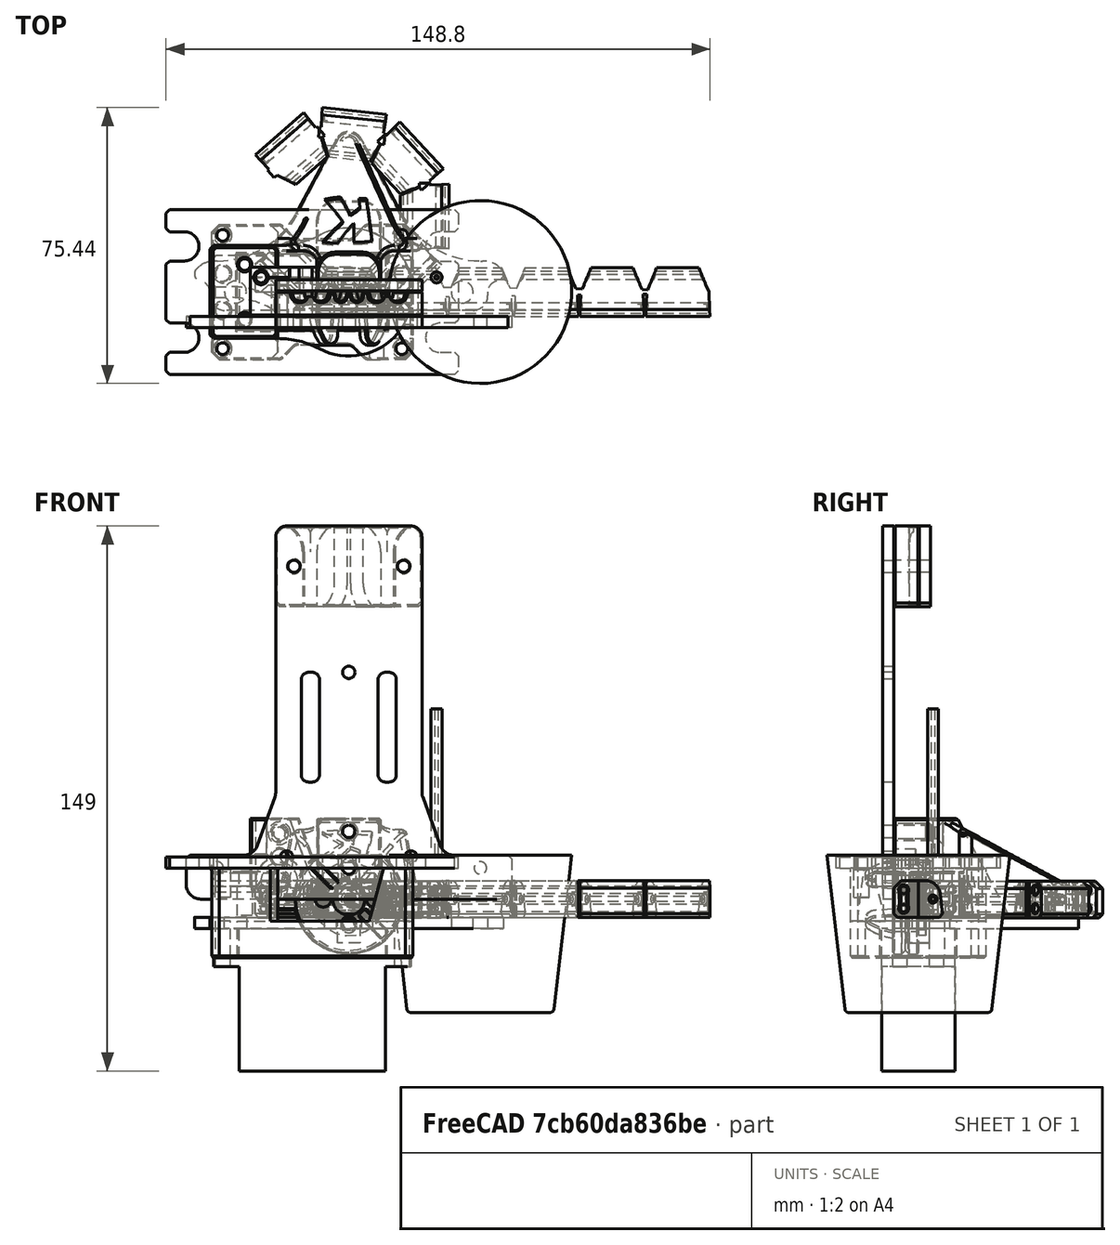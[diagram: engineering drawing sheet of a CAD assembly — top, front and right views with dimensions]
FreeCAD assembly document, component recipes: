
FREECAD ASSEMBLY — COMPONENT RECIPES ("finger-filaflex")

This assembly document has 2 components, labeled P0..P1 below (a component is one placed body or linked part). 1 of them carries a construction recipe — the FreeCAD feature program that regenerates the part from scratch, quoted from this document or its linked companion documents; the rest are supplied as boundary geometry only. No exploded tour is included for this assembly.
COMPONENT P0 — geometry summary ("EnsembleServo"; no construction recipe available for this part):
  bounding box: 80.0 x 61.5 x 45.0 mm
  tessellated surface: 38,648 triangles
  volume: 61605 mm^3 (28% of its bounding box)
COMPONENT P1 — recipe-attached ("finger-actuator", modeled in this document).
Construction recipe (the document's own serialized feature program — sketch geometry with constraints, then the solid features built on it; lengths are millimeters unless a unit is written):

FEATURE [Part::SubShapeBinder] Import004  label="Import004(Chamfer019)"
  BindCopyOnChange = 0
  BindMode = 0
  ClaimChildren = false
  Context = -> <external main-actuator.FCStd>#Part [Part005.Part003.Link008.Body011.Import004.]
  EdgeTolerance = 1e-06
  FillStyle = 0
  FixShape = 1
  Fuse = false
  InvalidShape = false
  MakeFace = false
  MergeEdges = true
  OffsetFill = false
  OffsetIntersection = false
  OffsetJoinType = 0
  OffsetOpenResult = false
  Outline = false
  PartialLoad = false
  Relative = true
  SplitEdges = false
  Support = -> [Part004[Body001.Chamfer019.]]
  TightBound = false
  TreeRank = 344
  ValidateShape = false
  _Version = 8
FEATURE [Sketcher::SketchObject] Sketch037
  ArcFitTolerance = 1e-06
  AttachmentSupport = -> [XZ_Plane016]
  ExternalBSplineMaxDegree = 5
  ExternalBSplineTolerance = 0.0001
  ExternalGeometry = -> [Import004]
  FixShape = 1
  FullyConstrained = true
  InternalTolerance = 1e-06
  InvalidShape = false
  MakeInternals = false
  MapMode = 5
  Placement = pos=(0,0,0) rot=(1,0,0;1.5708rad)
  Support = -> [XZ_Plane016]
  TreeRank = 343
  ValidateShape = false
  sketch-geometry (19):
    g0: LineSegment StartX=-44.5 StartY=0 StartZ=0 EndX=-44.5 EndY=12 EndZ=0
    g1: LineSegment StartX=-44.5 StartY=12 StartZ=0 EndX=-26 EndY=12 EndZ=0
    g2: LineSegment StartX=-26 StartY=12 StartZ=0 EndX=-20 EndY=28.4849 EndZ=0
    g3: LineSegment StartX=-20 StartY=28.4849 StartZ=0 EndX=-20 EndY=102 EndZ=0
    g4: LineSegment StartX=-20 StartY=102 StartZ=0 EndX=20 EndY=102 EndZ=0
    g5: LineSegment StartX=20 StartY=102 StartZ=0 EndX=20 EndY=28.4849 EndZ=0
    g6: LineSegment StartX=20 StartY=28.4849 StartZ=0 EndX=26 EndY=12 EndZ=0
    g7: LineSegment StartX=26 StartY=12 StartZ=0 EndX=44.5 EndY=12 EndZ=0
    g8: LineSegment StartX=44.5 StartY=12 StartZ=0 EndX=44.5 EndY=0 EndZ=0
    g9: LineSegment StartX=44.5 StartY=0 StartZ=0 EndX=-44.5 EndY=0 EndZ=0
    g10: Circle CenterX=0 CenterY=18.5 CenterZ=0 NormalX=0 NormalY=0 NormalZ=1 AngleXU=0 Radius=1.7
    g11: Circle CenterX=0 CenterY=8.5 CenterZ=0 NormalX=0 NormalY=0 NormalZ=1 AngleXU=0 Radius=1.7
    g12: Circle CenterX=17 CenterY=11.5 CenterZ=0 NormalX=0 NormalY=0 NormalZ=1 AngleXU=0 Radius=1.7
    g13: Circle CenterX=-17 CenterY=11.5 CenterZ=0 NormalX=0 NormalY=0 NormalZ=1 AngleXU=0 Radius=1.7
    g14: Circle CenterX=-36 CenterY=8.5 CenterZ=0 NormalX=0 NormalY=0 NormalZ=1 AngleXU=0 Radius=1.7
    g15: Circle CenterX=36 CenterY=8.5 CenterZ=0 NormalX=0 NormalY=0 NormalZ=1 AngleXU=0 Radius=1.7
    g16: Circle CenterX=0 CenterY=62 CenterZ=0 NormalX=0 NormalY=0 NormalZ=1 AngleXU=0 Radius=1.7
    g17: Circle CenterX=-15 CenterY=91 CenterZ=0 NormalX=0 NormalY=0 NormalZ=1 AngleXU=0 Radius=1.7
    g18: Circle CenterX=15 CenterY=91 CenterZ=0 NormalX=0 NormalY=0 NormalZ=1 AngleXU=0 Radius=1.7
  constraints (49):
    c: Vertical(g0)
    c: Coincident(g1,g0)
    c: Horizontal(g1)
    c: Coincident(g1,g2)
    c: Coincident(g2,g3)
    c: Vertical(g3)
    c: Coincident(g3,g4)
    c: Horizontal(g4)
    c: Coincident(g4,g5)
    c: Coincident(g5,g6)
    c: Coincident(g6,g7)
    c: Horizontal(g7)
    c: Coincident(g7,g8)
    c: Vertical(g8)
    c: Coincident(g8,g9)
    c: Coincident(g9,g0)
    c: Horizontal(g9)
    c: Symmetric(g0,g8,g-1)
    c: Symmetric(g1,g6,g-2)
    c: Symmetric(g2,g5,g-2)
    c: Vertical(g5)
    c: DistanceY(g-1,g1) = 12
    c: Angle(g2,g1) = 1.91986
    c: DistanceX(g0,g1) = 18.5
    c: DistanceX(g0,g-1) = 44.5
    c: PointOnObject(g10,g-2)
    c: PointOnObject(g11,g-2)
    c: Equal(g15,g12)
    c: Equal(g15,g10)
    c: Equal(g15,g11)
    c: Equal(g15,g13)
    c: Equal(g15,g14)
    c: Diameter(g15) = 3.4
    c: Symmetric(g13,g12,g-2)
    c: Symmetric(g14,g15,g-2)
    c: DistanceY(g11,g10) = 10
    c: DistanceY(g-1,g11) = 8.5
    c: Coincident(g14,g-3)
    c: Coincident(g13,g-4)
    c: PointOnObject(g16,g-2)
    c: Equal(g18,g17)
    c: Equal(g17,g16)
    c: Equal(g16,g12)
    c: Symmetric(g17,g18,g-2)
    c: DistanceX(g17,g18) = 30
    c: DistanceY(g16,g18) = 29
    c: DistanceY(g18,g4) = 11
    c: DistanceY(g-1,g4) = 102
    c: DistanceX(g4,g4) = 40
FEATURE [PartDesign::Pad] Pad012
  AddSubType = 0
  AlongSketchNormal = false
  AutoTaperInnerAngle = true
  CheckUpToFaceLimits = true
  ClaimChildren = false
  Direction = (0,-1,-2e-16)
  Fit = 0
  FitJoin = 0
  FixShape = 1
  InnerFit = 0
  InnerFitJoin = 0
  InvalidShape = false
  Length = 3
  Length2 = 10
  Linearize = true
  NewSolid = false
  Profile = -> Sketch037
  ReferenceAxis = -> Sketch037 [N_Axis]
  Refine = true
  Suppress = false
  TaperInnerAngle = 0
  TaperInnerAngleRev = 0
  TreeRank = 345
  Type = 0
  ValidateShape = false
  _ProfileBasedVersion = 1
FEATURE [PartDesign::Fillet] Fillet007
  AddSubType = 0
  Base = -> Pad012 [Edge26,Edge1]
  BaseFeature = -> Pad012
  FixShape = 1
  InvalidShape = false
  NewSolid = false
  Radius = 4
  Refine = true
  SupportTransform = false
  Suppress = false
  TreeRank = 346
  UseAllEdges = false
  ValidateShape = false
FEATURE [PartDesign::Fillet] Fillet008
  AddSubType = 0
  Base = -> Fillet007 [Edge54,Edge53,Edge48,Edge27]
  BaseFeature = -> Fillet007
  FixShape = 1
  InvalidShape = false
  NewSolid = false
  Radius = 4
  Refine = true
  SupportTransform = false
  Suppress = false
  TreeRank = 347
  UseAllEdges = false
  ValidateShape = false
FEATURE [PartDesign::Chamfer] Chamfer024
  AddSubType = 0
  Angle = 45
  Base = -> Fillet008 [Edge47,Edge27]
  BaseFeature = -> Fillet008
  ChamferType = 0
  FixShape = 1
  FlipDirection = false
  InvalidShape = false
  NewSolid = false
  Refine = true
  Size = 1
  Size2 = 1
  SupportTransform = false
  Suppress = false
  TreeRank = 348
  UseAllEdges = false
  ValidateShape = false
FEATURE [PartDesign::Fillet] Fillet012
  AddSubType = 0
  Base = -> Chamfer024 [Edge49,Edge45]
  BaseFeature = -> Chamfer024
  FixShape = 1
  InvalidShape = false
  NewSolid = false
  Radius = 3
  Refine = true
  SupportTransform = false
  Suppress = false
  TreeRank = 410
  UseAllEdges = false
  ValidateShape = false
FEATURE [Sketcher::SketchObject] Sketch040
  ArcFitTolerance = 1e-06
  AttachmentSupport = -> [XZ_Plane016]
  ExternalBSplineMaxDegree = 5
  ExternalBSplineTolerance = 0.0001
  ExternalGeometry = -> [Fillet012]
  FixShape = 1
  FullyConstrained = true
  InternalTolerance = 1e-06
  InvalidShape = false
  MakeInternals = false
  MapMode = 5
  Placement = pos=(0,0,0) rot=(1,0,0;1.5708rad)
  Support = -> [XZ_Plane016]
  TreeRank = 411
  ValidateShape = false
  sketch-geometry (10):
    g0: LineSegment StartX=13 StartY=32 StartZ=0 EndX=13 EndY=62 EndZ=0
    g1: LineSegment StartX=13 StartY=62 StartZ=0 EndX=8 EndY=62 EndZ=0
    g2: LineSegment StartX=8 StartY=62 StartZ=0 EndX=8 EndY=32 EndZ=0
    g3: LineSegment StartX=8 StartY=32 StartZ=0 EndX=13 EndY=32 EndZ=0
    g4: GeomPoint [constr] X=10.5 Y=47 Z=0
    g5: LineSegment StartX=-8 StartY=32 StartZ=0 EndX=-8 EndY=62 EndZ=0
    g6: LineSegment StartX=-8 StartY=62 StartZ=0 EndX=-13 EndY=62 EndZ=0
    g7: LineSegment StartX=-13 StartY=62 StartZ=0 EndX=-13 EndY=32 EndZ=0
    g8: LineSegment StartX=-13 StartY=32 StartZ=0 EndX=-8 EndY=32 EndZ=0
    g9: GeomPoint [constr] X=-10.5 Y=47 Z=0
  constraints (25):
    c: Coincident(g0,g1)
    c: Coincident(g1,g2)
    c: Coincident(g2,g3)
    c: Coincident(g3,g0)
    c: Horizontal(g1)
    c: Horizontal(g3)
    c: Vertical(g0)
    c: Vertical(g2)
    c: Symmetric(g1,g0,g4)
    c: Coincident(g5,g6)
    c: Coincident(g6,g7)
    c: Coincident(g7,g8)
    c: Coincident(g8,g5)
    c: Horizontal(g6)
    c: Horizontal(g8)
    c: Vertical(g5)
    c: Vertical(g7)
    c: Symmetric(g6,g5,g9)
    c: Symmetric(g9,g4,g-2)
    c: Equal(g5,g2)
    c: DistanceX(g6,g6) = 5
    c: Equal(g1,g6)
    c: DistanceY(g7,g7) = 30
    c: DistanceY(g9,g-3) = 15
    c: DistanceX(g5,g1) = 16
FEATURE [PartDesign::Pocket] Pocket018
  AddSubType = 1
  AlongSketchNormal = false
  AutoTaperInnerAngle = true
  BaseFeature = -> Fillet012
  CheckUpToFaceLimits = true
  ClaimChildren = false
  Direction = (0,1,2e-16)
  Fit = 0
  FitJoin = 0
  FixShape = 1
  InnerFit = 0
  InnerFitJoin = 0
  InvalidShape = false
  Length = 5
  Length2 = 10
  Linearize = true
  NewSolid = false
  Profile = -> Sketch040
  ReferenceAxis = -> Sketch040 [N_Axis]
  Refine = true
  Reversed = true
  Suppress = false
  TaperInnerAngle = 0
  TaperInnerAngleRev = 0
  TreeRank = 412
  Type = 1
  ValidateShape = false
  _ProfileBasedVersion = 1
  _Version = 1
FEATURE [PartDesign::Fillet] Fillet016
  AddSubType = 0
  Base = -> Pocket018 [Edge100,Edge98,Edge104,Edge102,Edge84,Edge82,Edge88,Edge86]
  BaseFeature = -> Pocket018
  FixShape = 1
  InvalidShape = false
  NewSolid = false
  Radius = 2
  Refine = true
  SupportTransform = false
  Suppress = false
  TreeRank = 423
  UseAllEdges = false
  ValidateShape = false
FEATURE [PartDesign::Body] Body011  label="PlaqueSupport"
  AutoGroupSolids = false
  ClaimAllChildren = false
  ExportMode = 0
  FixShape = 1
  Group = -> [Sketch037,Import004,Pad012,Fillet007,Fillet008,Chamfer024,Fillet012,Sketch040,Pocket018,Fillet016]
  InvalidShape = false
  Origin = -> Origin018
  Placement = pos=(0,-6.73,0) rot=(0,0,1;0rad)
  SingleSolid = true
  Tip = -> Fillet016
  TreeRank = 342
  ValidateShape = false
  _ExportChildren = -> [Import004,Pad012,Fillet007,Fillet008,Chamfer024,Fillet012,Pocket018,Fillet016]
  _GroupVersion = 1
FEATURE [Sketcher::SketchObject] Sketch043
  ArcFitTolerance = 1e-06
  AttachmentSupport = -> [XZ_Plane021]
  ExternalBSplineMaxDegree = 5
  ExternalBSplineTolerance = 0.0001
  FixShape = 1
  FullyConstrained = true
  InternalTolerance = 1e-06
  InvalidShape = false
  MakeInternals = false
  MapMode = 5
  Placement = pos=(0,0,0) rot=(1,0,0;1.5708rad)
  Support = -> [XZ_Plane021]
  TreeRank = 447
  ValidateShape = false
  sketch-geometry (7):
    g0: Circle CenterX=15 CenterY=-11 CenterZ=0 NormalX=0 NormalY=0 NormalZ=1 AngleXU=0 Radius=1.65
    g1: Circle CenterX=-15 CenterY=-11 CenterZ=0 NormalX=0 NormalY=0 NormalZ=1 AngleXU=0 Radius=1.65
    g2: LineSegment StartX=20 StartY=-22 StartZ=0 EndX=-20 EndY=-22 EndZ=0
    g3: LineSegment StartX=-20 StartY=-22 StartZ=0 EndX=-20 EndY=0 EndZ=0
    g4: LineSegment StartX=-20 StartY=0 StartZ=0 EndX=20 EndY=0 EndZ=0
    g5: LineSegment StartX=20 StartY=0 StartZ=0 EndX=20 EndY=-22 EndZ=0
    g6: LineSegment [constr] StartX=15 StartY=-11 StartZ=0 EndX=-20 EndY=-11 EndZ=0
  constraints (18):
    c: Symmetric(g1,g0,g-2)
    c: DistanceX(g1,g0) = 30
    c: Equal(g1,g0)
    c: Diameter(g1) = 3.3
    c: DistanceY(g1,g-1) = 11
    c: Coincident(g2,g3)
    c: Coincident(g3,g4)
    c: Coincident(g4,g5)
    c: Coincident(g5,g2)
    c: Horizontal(g2)
    c: Vertical(g3)
    c: Vertical(g5)
    c: Symmetric(g3,g4,g-2)
    c: DistanceX(g4,g4) = 40
    c: Coincident(g6,g0)
    c: Horizontal(g6)
    c: Symmetric(g2,g3,g6)
    c: PointOnObject(g3,g-1)
FEATURE [PartDesign::Pad] Pad016
  AddSubType = 0
  AlongSketchNormal = false
  AutoTaperInnerAngle = true
  CheckUpToFaceLimits = true
  ClaimChildren = false
  Direction = (0,-1,-2e-16)
  Fit = 0
  FitJoin = 0
  FixShape = 1
  InnerFit = 0
  InnerFitJoin = 0
  InvalidShape = false
  Length = 7
  Length2 = 10
  Linearize = true
  NewSolid = false
  Profile = -> Sketch043
  ReferenceAxis = -> Sketch043 [N_Axis]
  Refine = true
  Reversed = true
  Suppress = false
  TaperInnerAngle = 0
  TaperInnerAngleRev = 0
  TreeRank = 448
  Type = 0
  ValidateShape = true
  _ProfileBasedVersion = 1
FEATURE [PartDesign::Fillet] Fillet017
  AddSubType = 0
  Base = -> Pad016 [Edge5,Edge8]
  BaseFeature = -> Pad016
  FixShape = 1
  InvalidShape = false
  NewSolid = false
  Radius = 3
  Refine = true
  SupportTransform = false
  Suppress = false
  TreeRank = 449
  UseAllEdges = false
  ValidateShape = true
FEATURE [Sketcher::SketchObject] Sketch044
  ArcFitTolerance = 1e-06
  AttachmentSupport = -> [Fillet017]
  ExternalBSplineMaxDegree = 5
  ExternalBSplineTolerance = 0.0001
  ExternalGeometry = -> [Fillet017]
  FixShape = 1
  FullyConstrained = true
  InternalTolerance = 1e-06
  InvalidShape = false
  MakeInternals = false
  MapMode = 5
  Placement = pos=(0,7,0) rot=(0,0.707107,0.707107;3.14159rad)
  Support = -> [Fillet017]
  TreeRank = 450
  ValidateShape = false
  sketch-geometry (10):
    g0: ArcOfCircle CenterX=-20.5 CenterY=-7.07107 CenterZ=0 NormalX=0 NormalY=0 NormalZ=1 AngleXU=0 Radius=10 StartAngle=0 EndAngle=0.785398
    g1: ArcOfCircle CenterX=-0.5 CenterY=-7.07107 CenterZ=0 NormalX=0 NormalY=0 NormalZ=1 AngleXU=0 Radius=10 StartAngle=2.35619 EndAngle=3.14159
    g2: LineSegment StartX=-13.4289 StartY=-5.30859e-08 StartZ=0 EndX=-15.4289 EndY=2 EndZ=0
    g3: ArcOfCircle CenterX=-12.2 CenterY=-15.7459 CenterZ=0 NormalX=0 NormalY=0 NormalZ=1 AngleXU=0 Radius=10 StartAngle=5.60753 EndAngle=6.28319
    g4: LineSegment StartX=-4.39701 StartY=-22 StartZ=0 EndX=-6 EndY=-24 EndZ=0
    g5: LineSegment StartX=-7.57107 StartY=1e-16 StartZ=0 EndX=-5.57107 EndY=2 EndZ=0
    g6: LineSegment StartX=-10.5 StartY=-7.07107 StartZ=0 EndX=-10.5 EndY=-24 EndZ=0
    g7: LineSegment [constr] StartX=-15.4289 StartY=2 StartZ=0 EndX=0 EndY=2 EndZ=0
    g8: LineSegment [constr] StartX=-10.5 StartY=-24 StartZ=0 EndX=0 EndY=-24 EndZ=0
    g9: LineSegment StartX=-2.2 StartY=-15.7459 StartZ=0 EndX=-2.2 EndY=2 EndZ=0
  constraints (30):
    c: Tangent(g2,g0) = -1.5708
    c: Tangent(g5,g1) = 1.5708
    c: Tangent(g4,g3) = 1.5708
    c: DistanceY(g-1,g5) = 2
    c: Vertical(g6)
    c: Tangent(g6,g1)
    c: Tangent(g6,g0) = 1.5708
    c: Coincident(g7,g2)
    c: Horizontal(g7)
    c: PointOnObject(g7,g-2)
    c: PointOnObject(g5,g7)
    c: Coincident(g1,g0)
    c: Coincident(g8,g6)
    c: Horizontal(g8)
    c: PointOnObject(g4,g8)
    c: Equal(g1,g0)
    c: Equal(g1,g3)
    c: Radius(g1) = 10
    c: PointOnObject(g9,g7)
    c: Vertical(g9)
    c: Tangent(g9,g3) = -1.5708
    c: DistanceX(g9,g-1) = 2.2
    c: Perpendicular(g5,g2)
    c: Equal(g5,g2)
    c: DistanceX(g4,g8) = 6
    c: PointOnObject(g8,g-2)
    c: DistanceY(g8,g-3) = 2
    c: DistanceX(g6,g8) = 10.5
    c: PointOnObject(g3,g-3)
    c: DistanceY(g1,g5) = 2
FEATURE [Sketcher::SketchObject] Sketch045
  ArcFitTolerance = 1e-06
  AttachmentSupport = -> [Fillet017]
  ExternalBSplineMaxDegree = 5
  ExternalBSplineTolerance = 0.0001
  ExternalGeometry = -> [Sketch044]
  FixShape = 1
  FullyConstrained = true
  InternalTolerance = 1e-06
  InvalidShape = false
  MakeInternals = false
  MapMode = 5
  Placement = pos=(0,4.9e-15,-22) rot=(1,0,0;3.14159rad)
  Support = -> [Fillet017]
  TreeRank = 451
  ValidateShape = false
  sketch-geometry (5):
    g0: Circle [constr] CenterX=10.5 CenterY=-5.6 CenterZ=0 NormalX=0 NormalY=0 NormalZ=1 AngleXU=0 Radius=1.4
    g1: ArcOfCircle CenterX=10.5 CenterY=-5.6 CenterZ=0 NormalX=0 NormalY=0 NormalZ=1 AngleXU=0 Radius=1.4 StartAngle=0.221311 EndAngle=2.92027
    g2: LineSegment StartX=9.13415 StartY=-5.29267 StartZ=0 EndX=8.75 EndY=-7 EndZ=0
    g3: LineSegment StartX=8.75 StartY=-7 StartZ=0 EndX=12.25 EndY=-7 EndZ=0
    g4: LineSegment StartX=12.25 StartY=-7 StartZ=0 EndX=11.8659 EndY=-5.29269 EndZ=0
  constraints (14):
    c: PointOnObject(g-3,g0)
    c: Vertical(g0,g-3)
    c: Diameter(g0) = 2.8
    c: Coincident(g1,g0)
    c: PointOnObject(g1,g0)
    c: Coincident(g2,g1)
    c: Tangent(g2,g0)
    c: Coincident(g3,g2)
    c: Horizontal(g3)
    c: Coincident(g4,g3)
    c: Coincident(g4,g1)
    c: Tangent(g4,g0)
    c: Symmetric(g3,g2,g-3)
    c: DistanceX(g3,g3) = 3.5
FEATURE [PartDesign::SubtractivePipe] Pipe003
  AddSubType = 1
  AuxilleryCurvelinear = true
  AuxillerySpineTangent = false
  BaseFeature = -> Fillet017
  Binormal = (0,0,0)
  ClaimChildren = false
  Fit = 0
  FitJoin = 0
  FixShape = 1
  InnerFit = 0
  InnerFitJoin = 0
  InvalidShape = false
  Linearize = true
  Mode = 0
  MoveProfile = false
  NewSolid = false
  Profile = -> Sketch045
  Refine = true
  RotateProfile = false
  Spine = -> Sketch044 [Edge1,Edge2,Edge3]
  SpineTangent = false
  Suppress = false
  Transformation = 0
  Transition = 1
  TreeRank = 452
  ValidateShape = true
  _ProfileBasedVersion = 2
FEATURE [PartDesign::SubtractivePipe] Pipe004
  AddSubType = 1
  AuxilleryCurvelinear = true
  AuxillerySpineTangent = false
  BaseFeature = -> Pipe003
  Binormal = (0,0,0)
  ClaimChildren = false
  Fit = 0
  FitJoin = 0
  FixShape = 1
  InnerFit = 0
  InnerFitJoin = 0
  InvalidShape = false
  Linearize = true
  Mode = 0
  MoveProfile = false
  NewSolid = false
  Profile = -> Sketch045
  Refine = true
  RotateProfile = false
  Spine = -> Sketch044 [Edge5,Edge4,Edge3]
  SpineTangent = false
  Suppress = false
  Transformation = 0
  Transition = 1
  TreeRank = 453
  ValidateShape = true
  _ProfileBasedVersion = 2
FEATURE [Sketcher::SketchObject] Sketch046
  ArcFitTolerance = 1e-06
  AttachmentSupport = -> [XY_Plane021]
  ExternalBSplineMaxDegree = 5
  ExternalBSplineTolerance = 0.0001
  ExternalGeometry = -> [Sketch044]
  FixShape = 1
  FullyConstrained = true
  InternalTolerance = 1e-06
  InvalidShape = false
  MakeInternals = false
  MapMode = 5
  Support = -> [XY_Plane021]
  TreeRank = 454
  ValidateShape = false
  sketch-geometry (5):
    g0: Circle [constr] CenterX=2.2 CenterY=5.6 CenterZ=0 NormalX=0 NormalY=0 NormalZ=1 AngleXU=0 Radius=1.4
    g1: ArcOfCircle CenterX=2.2 CenterY=5.6 CenterZ=0 NormalX=0 NormalY=0 NormalZ=1 AngleXU=0 Radius=1.4 StartAngle=3.36292 EndAngle=6.06187
    g2: LineSegment StartX=0.834149 StartY=5.29267 StartZ=0 EndX=0.45 EndY=7 EndZ=0
    g3: LineSegment StartX=0.45 StartY=7 StartZ=0 EndX=3.95 EndY=7 EndZ=0
    g4: LineSegment StartX=3.95 StartY=7 StartZ=0 EndX=3.56585 EndY=5.29268 EndZ=0
  constraints (13):
    c: PointOnObject(g-3,g0)
    c: Vertical(g0,g-3)
    c: Diameter(g0) = 2.8
    c: Coincident(g1,g0)
    c: PointOnObject(g1,g0)
    c: Coincident(g2,g1)
    c: Tangent(g2,g0)
    c: Coincident(g2,g3)
    c: Horizontal(g3)
    c: Coincident(g3,g4)
    c: Symmetric(g3,g2,g-3)
    c: DistanceX(g3,g3) = 3.5
    c: Tangent(g4,g1) = 1.5708
FEATURE [PartDesign::SubtractivePipe] Pipe005
  AddSubType = 1
  AuxilleryCurvelinear = true
  AuxillerySpineTangent = false
  BaseFeature = -> Pipe004
  Binormal = (0,0,0)
  ClaimChildren = false
  Fit = 0
  FitJoin = 0
  FixShape = 1
  InnerFit = 0
  InnerFitJoin = 0
  InvalidShape = false
  Linearize = true
  Mode = 0
  MoveProfile = false
  NewSolid = false
  Profile = -> Sketch046
  Refine = true
  RotateProfile = false
  Spine = -> Sketch044 [Edge6,Edge7,Edge8]
  SpineTangent = false
  Suppress = false
  Transformation = 0
  Transition = 1
  TreeRank = 455
  ValidateShape = true
  _ProfileBasedVersion = 2
FEATURE [Sketcher::SketchObject] Sketch047
  ArcFitTolerance = 1e-06
  AttachmentSupport = -> [Pipe005]
  ExternalBSplineMaxDegree = 5
  ExternalBSplineTolerance = 0.0001
  ExternalGeometry = -> [Pipe005]
  FixShape = 1
  FullyConstrained = true
  InternalTolerance = 1e-06
  InvalidShape = false
  MakeInternals = false
  MapMode = 5
  Placement = pos=(0,7,0) rot=(0,0.707107,0.707107;3.14159rad)
  Support = -> [Pipe005]
  TreeRank = 456
  ValidateShape = false
  sketch-geometry (1):
    g0: Circle CenterX=-10.5 CenterY=-0.901586 CenterZ=0 NormalX=0 NormalY=0 NormalZ=1 AngleXU=0 Radius=2.5
  constraints (2):
    c: Coincident(g0,g-3)
    c: Diameter(g0) = 5
FEATURE [PartDesign::Pocket] Pocket020
  AddSubType = 1
  AlongSketchNormal = false
  AutoTaperInnerAngle = true
  BaseFeature = -> Pipe005
  CheckUpToFaceLimits = true
  ClaimChildren = false
  Direction = (0,-1,2e-16)
  Fit = 0
  FitJoin = 0
  FixShape = 1
  InnerFit = 0
  InnerFitJoin = 0
  InvalidShape = false
  Length = 1.5
  Length2 = 10
  Linearize = true
  NewSolid = false
  Profile = -> Sketch047
  ReferenceAxis = -> Sketch047 [N_Axis]
  Refine = true
  Suppress = false
  TaperInnerAngle = 0
  TaperInnerAngleRev = 0
  TreeRank = 457
  Type = 0
  ValidateShape = true
  _ProfileBasedVersion = 1
  _Version = 1
FEATURE [PartDesign::Mirrored] Mirrored
  AddSubType = 0
  BaseFeature = -> Pocket020
  CopyShape = false
  FixShape = 1
  InvalidShape = false
  MirrorPlane = -> Sketch045 [V_Axis]
  NewSolid = false
  OriginalSubs = -> [Pipe003,Pipe004,Pipe005,Pocket020]
  Originals = -> [Pipe003,Pipe004,Pipe005,Pocket020]
  ParallelTransform = true
  Refine = true
  SubTransform = true
  Suppress = false
  TreeRank = 458
  ValidateShape = true
  _Version = 3
FEATURE [PartDesign::Chamfer] Chamfer027
  AddSubType = 0
  Angle = 45
  Base = -> Mirrored [Edge51,Edge55,Edge59,Edge67,Edge49,Edge41,Edge29,Edge27,Edge22,Edge17]
  BaseFeature = -> Mirrored
  ChamferType = 0
  FixShape = 1
  FlipDirection = false
  InvalidShape = false
  NewSolid = false
  Refine = true
  Size = 0.4
  Size2 = 1
  SupportTransform = false
  Suppress = false
  TreeRank = 459
  UseAllEdges = false
  ValidateShape = true
FEATURE [PartDesign::Chamfer] Chamfer028
  AddSubType = 0
  Angle = 45
  Base = -> Chamfer027 [Edge7,Edge3]
  BaseFeature = -> Chamfer027
  ChamferType = 0
  FixShape = 1
  FlipDirection = false
  InvalidShape = false
  NewSolid = false
  Refine = true
  Size = 1
  Size2 = 1
  SupportTransform = false
  Suppress = false
  TreeRank = 460
  UseAllEdges = false
  ValidateShape = true
FEATURE [PartDesign::Chamfer] Chamfer029
  AddSubType = 0
  Angle = 45
  Base = -> Chamfer028 [Face2,Face9,Face5]
  BaseFeature = -> Chamfer028
  ChamferType = 0
  FixShape = 1
  FlipDirection = false
  InvalidShape = false
  NewSolid = false
  Refine = true
  Size = 0.4
  Size2 = 1
  SupportTransform = false
  Suppress = false
  TreeRank = 461
  UseAllEdges = false
  ValidateShape = true
FEATURE [PartDesign::Body] Body015  label="GestionnaireTube"
  AutoGroupSolids = false
  ClaimAllChildren = false
  ExportMode = 0
  FixShape = 1
  Group = -> [Sketch043,Pad016,Fillet017,Sketch044,Sketch045,Pipe003,Pipe004,Sketch046,Pipe005,Sketch047,Pocket020,Mirrored,Chamfer027,Chamfer028,Chamfer029]
  InvalidShape = false
  Origin = -> Origin024
  Placement = pos=(0,-6.7,102) rot=(0,0,1;0rad)
  SingleSolid = true
  Tip = -> Chamfer029
  TreeRank = 446
  ValidateShape = false
  _ExportChildren = -> [Pad016,Fillet017,Pipe003,Pipe004,Pipe005,Pocket020,Mirrored,Chamfer027,Chamfer028,Chamfer029]
  _GroupVersion = 1
FEATURE [Sketcher::SketchObject] Sketch048
  ArcFitTolerance = 1e-06
  AttachmentSupport = -> [XZ_Plane022]
  ExternalBSplineMaxDegree = 5
  ExternalBSplineTolerance = 0.0001
  FixShape = 1
  FullyConstrained = true
  InternalTolerance = 1e-06
  InvalidShape = false
  MakeInternals = false
  MapMode = 5
  Placement = pos=(0,0,0) rot=(1,0,0;1.5708rad)
  Support = -> [XZ_Plane022]
  TreeRank = 472
  ValidateShape = false
  sketch-geometry (7):
    g0: LineSegment StartX=20 StartY=-22 StartZ=0 EndX=20 EndY=0 EndZ=0
    g1: LineSegment StartX=20 StartY=0 StartZ=0 EndX=-20 EndY=0 EndZ=0
    g2: LineSegment StartX=-20 StartY=0 StartZ=0 EndX=-20 EndY=-22 EndZ=0
    g3: LineSegment StartX=-20 StartY=-22 StartZ=0 EndX=20 EndY=-22 EndZ=0
    g4: GeomPoint [constr] X=7e-16 Y=-11 Z=0
    g5: Circle CenterX=15 CenterY=-11 CenterZ=0 NormalX=0 NormalY=0 NormalZ=1 AngleXU=0 Radius=1.65
    g6: Circle CenterX=-15 CenterY=-11 CenterZ=0 NormalX=0 NormalY=0 NormalZ=1 AngleXU=0 Radius=1.65
  constraints (17):
    c: Coincident(g0,g1)
    c: Coincident(g1,g2)
    c: Coincident(g2,g3)
    c: Coincident(g3,g0)
    c: Horizontal(g1)
    c: Horizontal(g3)
    c: Vertical(g0)
    c: Vertical(g2)
    c: Symmetric(g1,g0,g4)
    c: DistanceX(g1,g1) = 40
    c: Symmetric(g1,g0,g-1)
    c: Equal(g5,g6)
    c: Diameter(g5) = 3.3
    c: Symmetric(g5,g6,g-2)
    c: DistanceX(g5) = 15
    c: DistanceY(g6,g1) = 11
    c: Horizontal(g4,g6)
FEATURE [PartDesign::Pad] Pad017
  AddSubType = 0
  AlongSketchNormal = false
  AutoTaperInnerAngle = true
  CheckUpToFaceLimits = true
  ClaimChildren = false
  Direction = (0,-1,-2e-16)
  Fit = 0
  FitJoin = 0
  FixShape = 1
  InnerFit = 0
  InnerFitJoin = 0
  InvalidShape = false
  Length = 3
  Length2 = 10
  Linearize = true
  NewSolid = false
  Profile = -> Sketch048
  ReferenceAxis = -> Sketch048 [N_Axis]
  Refine = true
  Reversed = true
  Suppress = false
  TaperInnerAngle = 0
  TaperInnerAngleRev = 0
  TreeRank = 473
  Type = 0
  ValidateShape = true
  _ProfileBasedVersion = 1
FEATURE [PartDesign::Fillet] Fillet018
  AddSubType = 0
  Base = -> Pad017 [Edge2,Edge5]
  BaseFeature = -> Pad017
  FixShape = 1
  InvalidShape = false
  NewSolid = false
  Radius = 3
  Refine = true
  SupportTransform = false
  Suppress = false
  TreeRank = 474
  UseAllEdges = false
  ValidateShape = true
FEATURE [PartDesign::Chamfer] Chamfer030
  AddSubType = 0
  Angle = 45
  Base = -> Fillet018 [Edge3,Edge14]
  BaseFeature = -> Fillet018
  ChamferType = 0
  FixShape = 1
  FlipDirection = false
  InvalidShape = false
  NewSolid = false
  Refine = true
  Size = 1
  Size2 = 1
  SupportTransform = false
  Suppress = false
  TreeRank = 475
  UseAllEdges = false
  ValidateShape = true
FEATURE [PartDesign::Body] Body016  label="PlaqueClipGestionnaire"
  AutoGroupSolids = false
  ClaimAllChildren = false
  ExportMode = 0
  FixShape = 1
  Group = -> [Sketch048,Pad017,Fillet018,Chamfer030]
  InvalidShape = false
  Origin = -> Origin025
  Placement = pos=(0,0.3,102) rot=(0,0,1;0rad)
  SingleSolid = true
  Tip = -> Chamfer030
  TreeRank = 471
  ValidateShape = false
  _ExportChildren = -> [Pad017,Fillet018,Chamfer030]
  _GroupVersion = 1
PROVENANCE & LICENSES
A FreeCAD (.FCStd) document from a public repository crawl; recipes are the document's own serialized feature recipes (and, for linked parts, companion documents' recipes).
License: as declared in the source repository (recorded in the dataset sidecar).
